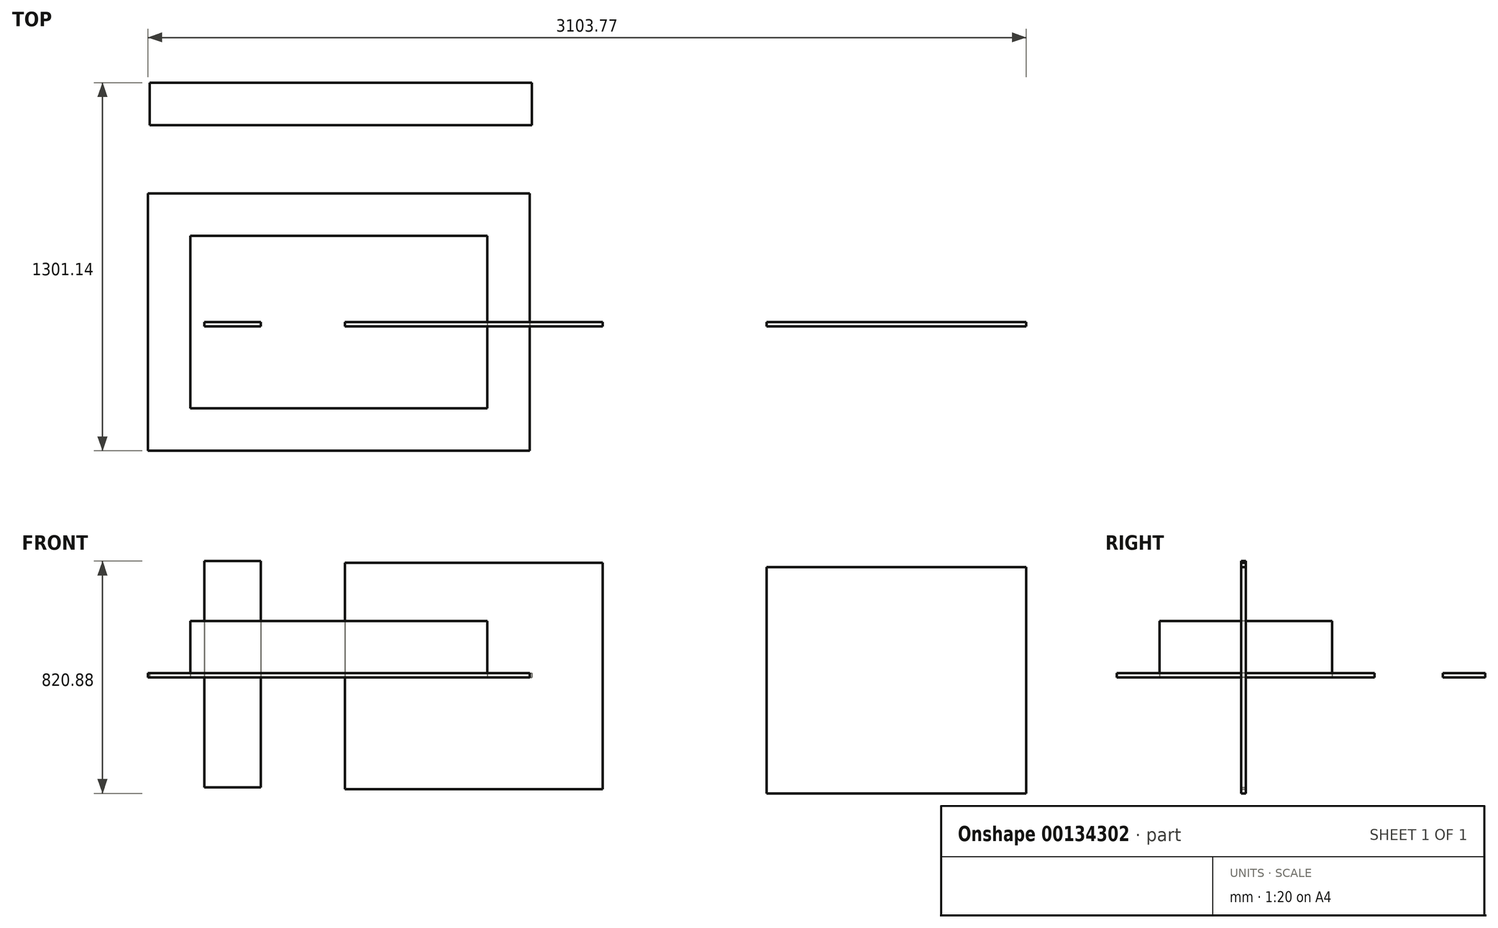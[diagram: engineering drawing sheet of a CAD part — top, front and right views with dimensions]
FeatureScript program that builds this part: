
annotation { "Feature Type Name" : "Feature", "Feature Type Description" : "" }
export const myFeature = defineFeature(function(context is Context, id is Id, definition is map)
    precondition{}
    {
        {
            assignVariable(context, id + "F0", {"name" : "mdf_thickness", "anyValue" : 16});
        }
        {
            var Q0;
            Q0=qCreatedBy(makeId("Top.planeOp"),FACE);
            var sketch = newSketch(context, id + "F1", { "sketchPlane" : qUnion([Q0])});
            skLineSegment(sketch, "E0.bottom", {"start": v(525, 305) * mm, "end": v(-525, 305) * mm});
            skLineSegment(sketch, "E0.top", {"start": v(525, -305) * mm, "end": v(-525, -305) * mm});
            skLineSegment(sketch, "E0.left", {"start": v(525, 305) * mm, "end": v(525, -305) * mm});
            skLineSegment(sketch, "E0.right", {"start": v(-525, 305) * mm, "end": v(-525, -305) * mm});
            skPoint(sketch, "E0.middle", {"position": v(0, 0) * mm});
            skLineSegment(sketch, "E1.bottom", {"start": v(-675, 455) * mm, "end": v(675, 455) * mm});
            skLineSegment(sketch, "E1.top", {"start": v(-675, -455) * mm, "end": v(675, -455) * mm});
            skLineSegment(sketch, "E1.left", {"start": v(-675, 455) * mm, "end": v(-675, -455) * mm});
            skLineSegment(sketch, "E1.right", {"start": v(675, 455) * mm, "end": v(675, -455) * mm});
            skLineSegment(sketch, "E2.bottom", {"start": v(-668.25, 846.14) * mm, "end": v(681.75, 846.14) * mm});
            skLineSegment(sketch, "E2.top", {"start": v(-668.25, 696.14) * mm, "end": v(681.75, 696.14) * mm});
            skLineSegment(sketch, "E2.left", {"start": v(-668.25, 846.14) * mm, "end": v(-668.25, 696.14) * mm});
            skLineSegment(sketch, "E2.right", {"start": v(681.75, 846.14) * mm, "end": v(681.75, 696.14) * mm});
            skSolve(sketch);
        }
        {
            var Q0;
            Q0=makeQuery(id+"F1.imprint","IMPRINT",FACE,{"disambiguationData":[TD([[makeQuery(id+"F1.imprint","IMPRINT",EDGE,{"derivedFrom":sQuery(id+"F1.wireOp",EDGE,"E2.bottom")}),-1.0]])]});
            extrude(context, id + "F2", {"entities" : qUnion([Q0]), "depth" : (getVariable(context, 'mdf_thickness')) * mm});
        }
        {
            var Q0;
            Q0=makeQuery(id+"F1.imprint","IMPRINT",FACE,{"disambiguationData":[TD([[makeQuery(id+"F1.imprint","IMPRINT",EDGE,{"derivedFrom":sQuery(id+"F1.wireOp",EDGE,"E0.bottom")}),-1.0]])]});
            var Q1;
            Q1=makeQuery(id+"F1.imprint","IMPRINT",FACE,{"disambiguationData":[TD([[makeQuery(id+"F1.imprint","IMPRINT",EDGE,{"derivedFrom":sQuery(id+"F1.wireOp",EDGE,"E0.bottom")}),1.0]])]});
            extrude(context, id + "F3", {"entities" : qUnion([Q0, Q1]), "depth" : (getVariable(context, 'mdf_thickness')) * mm});
        }
        {
            var Q0;
            Q0=qCreatedBy(makeId("Front.planeOp"),FACE);
            var sketch = newSketch(context, id + "F4", { "sketchPlane" : qUnion([Q0])});
            skLineSegment(sketch, "E3.bottom", {"start": v(-475.36, 411.34) * mm, "end": v(-275.36, 411.34) * mm});
            skLineSegment(sketch, "E3.top", {"start": v(-475.36, -388.66) * mm, "end": v(-275.36, -388.66) * mm});
            skLineSegment(sketch, "E3.left", {"start": v(-475.36, 411.34) * mm, "end": v(-475.36, -388.66) * mm});
            skLineSegment(sketch, "E3.right", {"start": v(-275.36, 411.34) * mm, "end": v(-275.36, -388.66) * mm});
            skLineSegment(sketch, "E4.bottom", {"start": v(21.87, 405.03) * mm, "end": v(931.87, 405.03) * mm});
            skLineSegment(sketch, "E4.top", {"start": v(21.87, -394.97) * mm, "end": v(931.87, -394.97) * mm});
            skLineSegment(sketch, "E4.left", {"start": v(21.87, 405.03) * mm, "end": v(21.87, -394.97) * mm});
            skLineSegment(sketch, "E4.right", {"start": v(931.87, 405.03) * mm, "end": v(931.87, -394.97) * mm});
            skLineSegment(sketch, "E5.bottom", {"start": v(1510.77, 390.46) * mm, "end": v(2428.77, 390.46) * mm});
            skLineSegment(sketch, "E5.top", {"start": v(1510.77, -409.54) * mm, "end": v(2428.77, -409.54) * mm});
            skLineSegment(sketch, "E5.left", {"start": v(1510.77, 390.46) * mm, "end": v(1510.77, -409.54) * mm});
            skLineSegment(sketch, "E5.right", {"start": v(2428.77, 390.46) * mm, "end": v(2428.77, -409.54) * mm});
            skSolve(sketch);
        }
        {
            var Q0;
            Q0=makeQuery(id+"F4.imprint","IMPRINT",FACE,{"disambiguationData":[TD([[makeQuery(id+"F4.imprint","IMPRINT",EDGE,{"derivedFrom":sQuery(id+"F4.wireOp",EDGE,"E3.bottom")}),-1.0]])]});
            extrude(context, id + "F5", {"entities" : qUnion([Q0]), "depth" : (getVariable(context, 'mdf_thickness')) * mm});
        }
        {
            var Q0;
            Q0=makeQuery(id+"F4.imprint","IMPRINT",FACE,{"disambiguationData":[TD([[makeQuery(id+"F4.imprint","IMPRINT",EDGE,{"derivedFrom":sQuery(id+"F4.wireOp",EDGE,"E4.bottom")}),-1.0]])]});
            extrude(context, id + "F6", {"entities" : qUnion([Q0]), "depth" : (getVariable(context, 'mdf_thickness')) * mm});
        }
        {
            var Q0;
            Q0=makeQuery(id+"F4.imprint","IMPRINT",FACE,{"disambiguationData":[TD([[makeQuery(id+"F4.imprint","IMPRINT",EDGE,{"derivedFrom":sQuery(id+"F4.wireOp",EDGE,"E5.bottom")}),-1.0]])]});
            extrude(context, id + "F7", {"entities" : qUnion([Q0]), "depth" : (getVariable(context, 'mdf_thickness')) * mm});
        }
        {
            var Q0;
            Q0=makeQuery(id+"F1.imprint","IMPRINT",FACE,{"disambiguationData":[TD([[makeQuery(id+"F1.imprint","IMPRINT",EDGE,{"derivedFrom":sQuery(id+"F1.wireOp",EDGE,"E0.bottom")}),1.0]])]});
            extrude(context, id + "F8", {"entities" : qUnion([Q0]), "depth" : 200 * mm});
        }
    });
